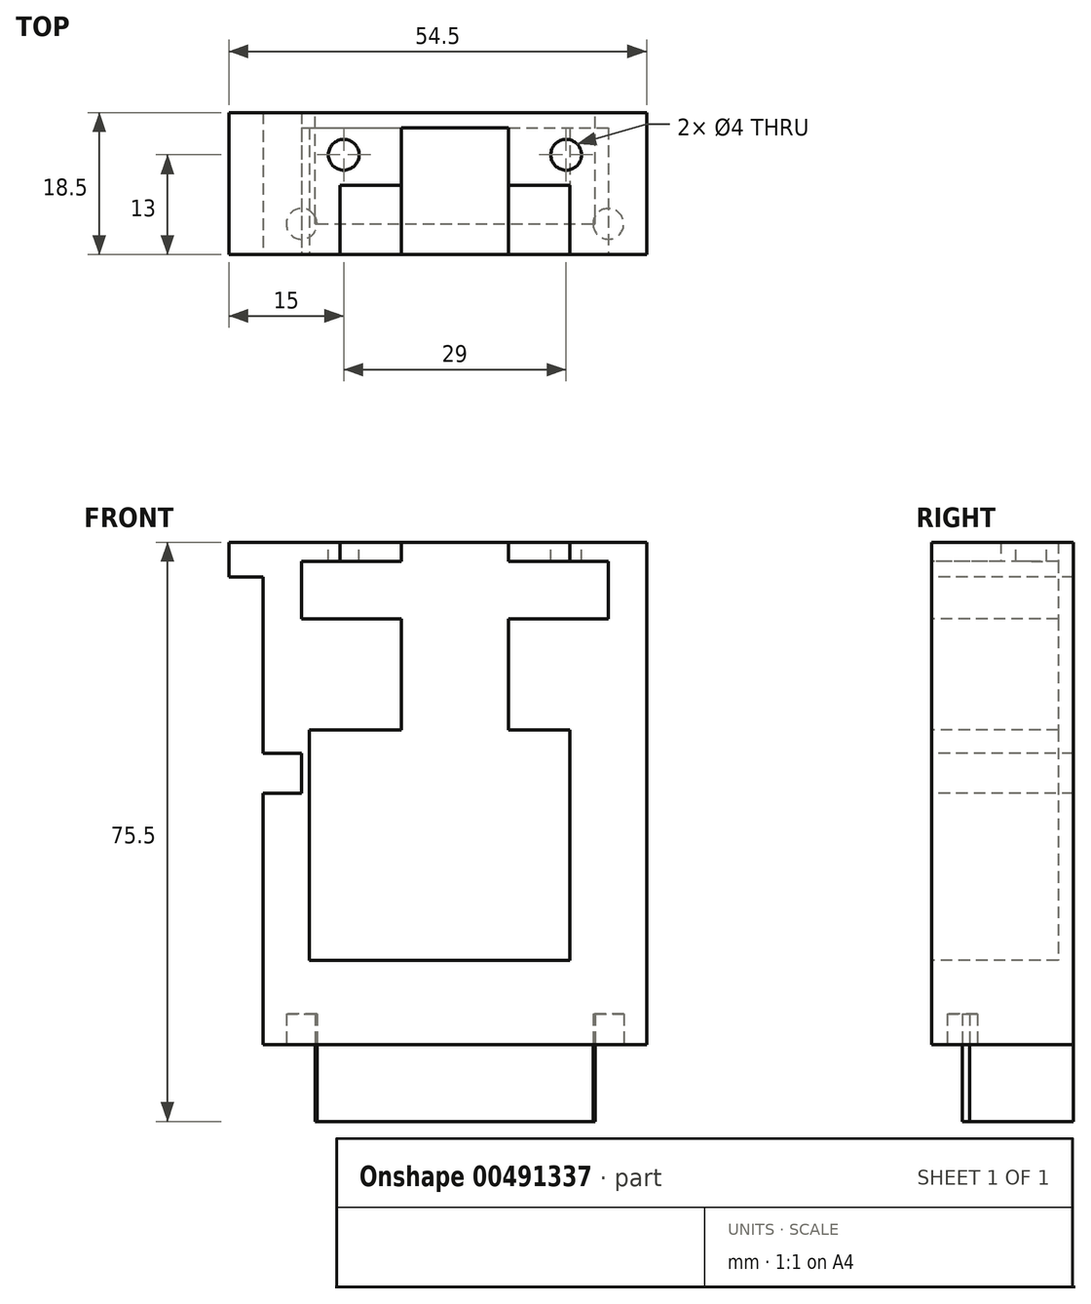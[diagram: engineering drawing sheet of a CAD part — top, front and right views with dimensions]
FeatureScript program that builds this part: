
annotation { "Feature Type Name" : "Feature", "Feature Type Description" : "" }
export const myFeature = defineFeature(function(context is Context, id is Id, definition is map)
    precondition{}
    {
        {
            var Q0;
            Q0=qCreatedBy(makeId("Top.planeOp"),FACE);
            var sketch = newSketch(context, id + "F0", { "sketchPlane" : qUnion([Q0])});
            skLineSegment(sketch, "E0.bottom", {"start": v(0, 9.25) * mm, "end": v(50, 9.25) * mm});
            skLineSegment(sketch, "E0.top", {"start": v(0, -9.25) * mm, "end": v(50, -9.25) * mm});
            skLineSegment(sketch, "E0.left", {"start": v(0, 9.25) * mm, "end": v(0, -9.25) * mm});
            skLineSegment(sketch, "E0.right", {"start": v(50, 9.25) * mm, "end": v(50, -9.25) * mm});
            skSolve(sketch);
        }
        {
            var Q0;
            Q0 = qSketchRegion(id + "F0", true);
            extrude(context, id + "F1", {"entities" : qUnion([Q0]), "endBound" : BoundingType.SYMMETRIC, "depth" : 65.5 * mm, "offsetDistance" : 25 * mm});
        }
        {
            var Q0;
            Q0=makeQuery(id+"F1.opExtrude","CAP_FACE",FACE,{"disambiguationData":[OSD([sQuery(id+"F0.wireOp",EDGE,"E0.bottom"),sQuery(id+"F0.wireOp",EDGE,"E0.top"),sQuery(id+"F0.wireOp",EDGE,"E0.left"),sQuery(id+"F0.wireOp",EDGE,"E0.right")])],"isStart":false});
            var sketch = newSketch(context, id + "F2", { "sketchPlane" : qUnion([Q0])});
            skCircle(sketch, "E1", {"center": v(10.5, 3.75) * mm, "radius": 2 * mm});
            skCircle(sketch, "E2.1.0.0", {"center": v(39.5, 3.75) * mm, "radius": 2 * mm});
            skLineSegment(sketch, "E3.bottom", {"start": v(10, -0.25) * mm, "end": v(40, -0.25) * mm});
            skLineSegment(sketch, "E3.top", {"start": v(10, -9.25) * mm, "end": v(40, -9.25) * mm});
            skLineSegment(sketch, "E3.left", {"start": v(10, -0.25) * mm, "end": v(10, -9.25) * mm});
            skLineSegment(sketch, "E3.right", {"start": v(40, -0.25) * mm, "end": v(40, -9.25) * mm});
            skSolve(sketch);
        }
        {
            var Q0;
            Q0 = qSketchRegion(id + "F2", true);
            extrude(context, id + "F3", {"entities" : qUnion([Q0]), "operationType" : NewBodyOperationType.REMOVE, "oppositeDirection" : true, "depth" : 4 * mm, "offsetDistance" : 25 * mm});
        }
        {
            var Q0;
            Q0=makeQuery(id+"F1.opExtrude","CAP_FACE",FACE,{"disambiguationData":[OSD([sQuery(id+"F0.wireOp",EDGE,"E0.bottom"),sQuery(id+"F0.wireOp",EDGE,"E0.top"),sQuery(id+"F0.wireOp",EDGE,"E0.left"),sQuery(id+"F0.wireOp",EDGE,"E0.right")])],"isStart":true});
            var sketch = newSketch(context, id + "F4", { "sketchPlane" : qUnion([Q0])});
            skCircle(sketch, "E4", {"center": v(5, 5.25) * mm, "radius": 2 * mm});
            skCircle(sketch, "E5.1.0.0", {"center": v(45, 5.25) * mm, "radius": 2 * mm});
            skLineSegment(sketch, "E5.direction1", {"start": v(5, 5.25) * mm, "end": v(45, 5.25) * mm, "construction": true});
            skLineSegment(sketch, "E6.bottom", {"start": v(6.75, 5.25) * mm, "end": v(43.25, 5.25) * mm});
            skLineSegment(sketch, "E6.top", {"start": v(6.75, -9.25) * mm, "end": v(43.25, -9.25) * mm});
            skLineSegment(sketch, "E6.left", {"start": v(6.75, 5.25) * mm, "end": v(6.75, -9.25) * mm});
            skLineSegment(sketch, "E6.right", {"start": v(43.25, 5.25) * mm, "end": v(43.25, -9.25) * mm});
            skSolve(sketch);
        }
        {
            var Q0;
            {var subQ5=sQuery(id+"F4.wireOp",EDGE,"E6.top");Q0=makeQuery(id+"F4.imprint","IMPRINT",FACE,{"disambiguationData":[TD([[makeQuery(id+"F4.imprint","IMPRINT",EDGE,{"derivedFrom":subQ5}),1.0]])]});}
            extrude(context, id + "F5", {"entities" : qUnion([Q0]), "operationType" : NewBodyOperationType.ADD, "depth" : 10 * mm, "offsetDistance" : 25 * mm});
        }
        {
            var Q0;
            {var subQ0=sQuery(id+"F4.wireOp",EDGE,"E6.bottom");var subQ1=sQuery(id+"F4.wireOp",EDGE,"E4");var subQ2=makeQuery(id+"F4.imprint","INTERSECT",VERTEX,{"derivedFrom":[subQ1,subQ0]});Q0=makeQuery(id+"F4.imprint","IMPRINT",FACE,{"disambiguationData":[TD([[makeQuery(id+"F4.imprint","IMPRINT",EDGE,{"disambiguationData":[TD([[subQ2,-1.0]])],"derivedFrom":subQ1}),1.0]])]});}
            var Q1;
            {var subQ0=sQuery(id+"F4.wireOp",EDGE,"E6.bottom");var subQ1=sQuery(id+"F4.wireOp",EDGE,"E5.1.0.0");var subQ2=makeQuery(id+"F4.imprint","INTERSECT",VERTEX,{"derivedFrom":[subQ1,subQ0]});Q1=makeQuery(id+"F4.imprint","IMPRINT",FACE,{"disambiguationData":[TD([[makeQuery(id+"F4.imprint","IMPRINT",EDGE,{"disambiguationData":[TD([[subQ2,1.0]])],"derivedFrom":subQ1}),1.0]])]});}
            var Q2;
            Q2=sQuery(id+"F4.wireOp",EDGE,"E4");
            var Q3;
            Q3=sQuery(id+"F4.wireOp",EDGE,"E5.1.0.0");
            extrude(context, id + "F6", {"entities" : qUnion([Q0, Q1]), "operationType" : NewBodyOperationType.REMOVE, "surfaceEntities" : qUnion([Q2, Q3]), "oppositeDirection" : true, "depth" : 4 * mm, "offsetDistance" : 25 * mm});
        }
        {
            var Q0;
            Q0=makeQuery(id+"F1.opExtrude","SWEPT_FACE",FACE,{"disambiguationData":[OSD([sQuery(id+"F0.wireOp",EDGE,"E0.top")])]});
            var sketch = newSketch(context, id + "F7", { "sketchPlane" : qUnion([Q0])});
            skLineSegment(sketch, "E7.bottom", {"start": v(6, 8.25) * mm, "end": v(40, 8.25) * mm});
            skLineSegment(sketch, "E7.top", {"start": v(6, -21.75) * mm, "end": v(40, -21.75) * mm});
            skLineSegment(sketch, "E7.left", {"start": v(6, 8.25) * mm, "end": v(6, -21.75) * mm});
            skLineSegment(sketch, "E7.right", {"start": v(40, 8.25) * mm, "end": v(40, -21.75) * mm});
            skLineSegment(sketch, "E8.bottom", {"start": v(18, 32.75) * mm, "end": v(32, 32.75) * mm});
            skLineSegment(sketch, "E8.top", {"start": v(18, 8.25) * mm, "end": v(32, 8.25) * mm});
            skLineSegment(sketch, "E8.left", {"start": v(18, 32.75) * mm, "end": v(18, 8.25) * mm});
            skLineSegment(sketch, "E8.right", {"start": v(32, 32.75) * mm, "end": v(32, 8.25) * mm});
            skLineSegment(sketch, "E9.bottom", {"start": v(5, 30.25) * mm, "end": v(45, 30.25) * mm});
            skLineSegment(sketch, "E9.top", {"start": v(5, 22.75) * mm, "end": v(45, 22.75) * mm});
            skLineSegment(sketch, "E9.left", {"start": v(5, 30.25) * mm, "end": v(5, 22.75) * mm});
            skLineSegment(sketch, "E9.right", {"start": v(45, 30.25) * mm, "end": v(45, 22.75) * mm});
            skSolve(sketch);
        }
        {
            var Q0;
            Q0 = qSketchRegion(id + "F7", true);
            extrude(context, id + "F8", {"entities" : qUnion([Q0]), "operationType" : NewBodyOperationType.REMOVE, "oppositeDirection" : true, "depth" : 16.5 * mm, "offsetDistance" : 25 * mm});
        }
        {
            var Q0;
            Q0=makeQuery(id+"F1.opExtrude","SWEPT_FACE",FACE,{"disambiguationData":[OSD([sQuery(id+"F0.wireOp",EDGE,"E0.left")])]});
            var sketch = newSketch(context, id + "F9", { "sketchPlane" : qUnion([Q0])});
            skLineSegment(sketch, "E10.bottom", {"start": v(-9.25, 32.75) * mm, "end": v(9.25, 32.75) * mm});
            skLineSegment(sketch, "E10.top", {"start": v(-9.25, 28.25) * mm, "end": v(9.25, 28.25) * mm});
            skLineSegment(sketch, "E10.left", {"start": v(-9.25, 32.75) * mm, "end": v(-9.25, 28.25) * mm});
            skLineSegment(sketch, "E10.right", {"start": v(9.25, 32.75) * mm, "end": v(9.25, 28.25) * mm});
            skLineSegment(sketch, "E11.bottom", {"start": v(-9.25, 5.25) * mm, "end": v(9.25, 5.25) * mm});
            skLineSegment(sketch, "E11.top", {"start": v(-9.25, 0) * mm, "end": v(9.25, 0) * mm});
            skLineSegment(sketch, "E11.left", {"start": v(-9.25, 5.25) * mm, "end": v(-9.25, 0) * mm});
            skLineSegment(sketch, "E11.right", {"start": v(9.25, 5.25) * mm, "end": v(9.25, 0) * mm});
            skLineSegment(sketch, "E12.bottom", {"start": v(4.2, 9.12) * mm, "end": v(4.55, 9.12) * mm});
            skLineSegment(sketch, "E12.top", {"start": v(4.2, 9.18) * mm, "end": v(4.55, 9.18) * mm});
            skLineSegment(sketch, "E12.left", {"start": v(4.2, 9.12) * mm, "end": v(4.2, 9.18) * mm});
            skLineSegment(sketch, "E12.right", {"start": v(4.55, 9.12) * mm, "end": v(4.55, 9.18) * mm});
            skSolve(sketch);
        }
        {
            var Q0;
            Q0=makeQuery(id+"F9.imprint","IMPRINT",FACE,{"disambiguationData":[TD([[makeQuery(id+"F9.imprint","IMPRINT",EDGE,{"derivedFrom":sQuery(id+"F9.wireOp",EDGE,"E10.bottom")}),-1.0]])]});
            extrude(context, id + "F10", {"entities" : qUnion([Q0]), "operationType" : NewBodyOperationType.ADD, "depth" : 4.5 * mm, "offsetDistance" : 25 * mm});
        }
        {
            var Q0;
            Q0=makeQuery(id+"F9.imprint","IMPRINT",FACE,{"disambiguationData":[TD([[makeQuery(id+"F9.imprint","IMPRINT",EDGE,{"derivedFrom":sQuery(id+"F9.wireOp",EDGE,"E11.bottom")}),-1.0]])]});
            extrude(context, id + "F11", {"entities" : qUnion([Q0]), "operationType" : NewBodyOperationType.REMOVE, "oppositeDirection" : true, "depth" : 5 * mm, "offsetDistance" : 25 * mm});
        }
    });
